# Revit family: LBA7
name_source: partatom
category: Equipement spécialisé
revit_build: Autodesk Revit 2017 (Build: 20160225_1515(x64)
units: mm (PartAtom-declared; Revit-internal decimal feet)

## family parameters
Basée sur le plan de construction = Non
Cote de connecteur circulaire = Utiliser le diamètre
Couper avec des vides une fois chargée = Non
Partagée = Non
Point de calcul de pièce = Non
Toujours verticalement = Oui
Type d'élément = Normal

## types (3) — shared parameters
Fabricant = La Barrière Automatique
URL = https://barriere-automatique.com
Visibilité_Support = Oui
diamètre_bareau_GA = 25 mm  [stored 0.082021 ft]
diamètre_grillage_GA = 15 mm  [stored 0.0492126 ft]
distance lisse du borne = 225 mm  [stored 0.738189 ft]
décalage sous lisse_GA = 104 mm
epaisseur_lisse = 57 mm  [stored 0.187008 ft]
epaisseur_repose_barrière_V = 100 mm  [stored 0.328084 ft]
h_GA = 728 mm  [stored 2.38845 ft]
h_axe_chapeau = 112 mm  [stored 0.367454 ft]
h_chapeau = 916 mm
h_repose_barrière = 874 mm  [stored 2.86745 ft]
hauteur_lisse = 84 mm  [stored 0.275591 ft]
largeur_borne = 360 mm  [stored 1.1811 ft]
largeur_chapeau = 365 mm  [stored 1.19751 ft]
longueur_borne = 360 mm  [stored 1.1811 ft]
longueur_chapeau = 365 mm  [stored 1.19751 ft]
longueur_lisse_attaché au borne = 150 mm
matériau_bandeaux_rouge = Plastique, rouge reflet
matériau_base = BLANC_MAT
matériau_borne = Stratifié, bleu marine
matériau_chapeau = BLANC_MAT
matériau_lisse = BLANC_MAT
matériau_répose_barrière = POSTE SUPPORT
origine_GA = 150 mm
position_grille1_GA = 200 mm  [stored 0.656168 ft]

## per-type parameters (varying)
| type | Modèle | Nombre_barreaux_GA | Visibilité_Grillage | W | distance_entre_grillage_GA | entreaxe_massifs | grille_type | hauteur_GTH | longueur_GA | longueur_lisse |
| LBA7_lise_ovale 7000mm | LBA  7 | 10 | Non | 260 mm  [stored 0.853018 ft] | 350 mm  [stored 1.14829 ft] | 7161 mm | lisse_ovale_GA_LBA : rideau pour lisse | 1000 mm  [stored 3.28084 ft] | 6850 mm  [stored 22.4738 ft] | 7000 mm  [stored 22.9659 ft] |
| LBA7_lise_ovale GTH 4000mm | LBA 7 GTH | 8 | Oui | 231 mm | 400 mm  [stored 1.31234 ft] | 4175 mm  [stored 13.6975 ft] | lisse_ovale_GTH_LBA : rideau pour lisse | 1740 mm  [stored 5.70866 ft] | 3850 mm  [stored 12.6312 ft] | 4000 mm  [stored 13.1234 ft] |
| LBA7_lisse_ovale GA 5000mm | LBA 7 GA | 11 | Oui | 260 mm  [stored 0.853018 ft] | 380 mm  [stored 1.24672 ft] | 5200 mm  [stored 17.0604 ft] | lisse_ovale_GA_LBA : rideau pour lisse | 1000 mm  [stored 3.28084 ft] | 4850 mm | 5000 mm  [stored 16.4042 ft] |

note: [stored X ft] marks values corroborated as IEEE doubles in the binary element streams (Revit-internal decimal feet)
